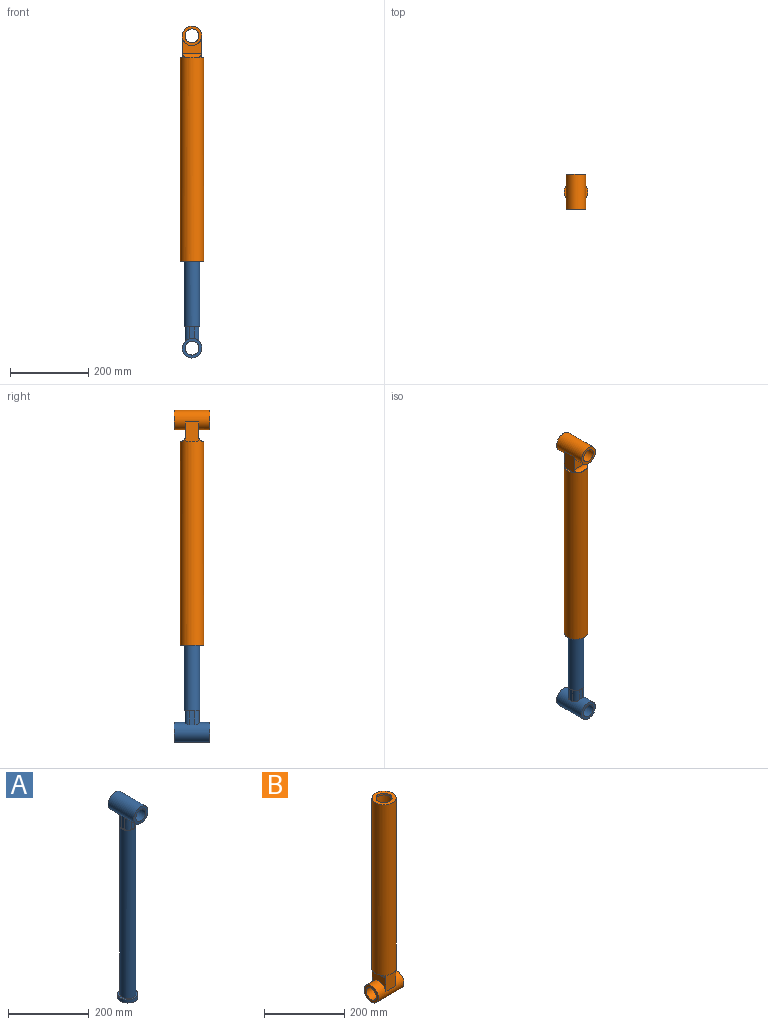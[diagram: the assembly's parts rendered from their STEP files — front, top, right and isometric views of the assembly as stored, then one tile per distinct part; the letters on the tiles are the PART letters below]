
ASSEMBLY  parts=2 mates=1
PART A: 24 faces, bbox 50.2x90x600 mm
  f0: cylinder r=17.5mm len=90mm, axis (0,-1,0), area 9896mm2, adj f18,f19
  f1: cylinder r=25mm len=90mm, axis (0,1,0), area 13084.8mm2, adj f4,f5,f6,f7,f18,f19,f20,f21
  f2: cylinder r=25mm len=50mm, axis (0,0,1), area 1570.8mm2, adj f12,f13
  f3: cylinder r=20mm len=510mm, axis (0,0,1), area 64088.5mm2, adj f8,f9,f10,f11,f13,f14,f15,f16
  f4: plane 36.96x11.71mm, normal (1,0,0), area 432.8mm2, adj f1,f8,f20,f21
  f5: plane 30.66x11mm, normal (0,1,0), area 332.2mm2, adj f1,f11,f20,f23
  f6: plane 37.34x11.71mm, normal (-1,0,0), area 437.2mm2, adj f1,f10,f22,f23
  f7: plane 30.66x11mm, normal (0,-1,0), area 332.2mm2, adj f1,f9,f21,f22
  f8: plane 27.16x5.32mm, normal (0,0,1), area 36.4mm2, adj f3,f4,f20,f21
  f9: plane 25.27x4.5mm, normal (0,0,1), area 28.9mm2, adj f3,f7,f21,f22
  f10: plane 27.16x5.32mm, normal (0,0,1), area 36.4mm2, adj f3,f6,f22,f23
  f11: plane 25.27x4.5mm, normal (0,0,1), area 28.9mm2, adj f3,f5,f20,f23
  f12: plane 50x50mm, normal (0,0,-1), area 1963.5mm2, adj f2
  f13: plane 50x50mm, normal (0,0,1), area 706.9mm2, adj f2,f3
  f14: plane 2.05x1.92mm, normal (0,0,-1), area 0.1mm2, adj f3,f22
  f15: plane 2.05x1.92mm, normal (0,0,-1), area 0.1mm2, adj f3,f21
  f16: plane 2.05x1.92mm, normal (0,0,-1), area 0.1mm2, adj f3,f20
  f17: plane 2.05x1.92mm, normal (0,0,-1), area 0.1mm2, adj f3,f23
  f18: plane 50x50mm, normal (0,-1,0), area 1001.4mm2, adj f0,f1
  f19: plane 50x50mm, normal (0,1,0), area 1001.4mm2, adj f0,f1
  f20: cylinder r=12mm len=36.96mm, axis (0,0,-1), area 636.4mm2, adj f1,f4,f5,f8,f11,f16
  f21: cylinder r=12mm len=36.96mm, axis (0,0,-1), area 636.4mm2, adj f1,f4,f7,f8,f9,f15
  f22: cylinder r=12mm len=37.34mm, axis (0,0,-1), area 640.9mm2, adj f1,f6,f7,f9,f10,f14
  f23: cylinder r=12mm len=37.34mm, axis (0,0,-1), area 640.9mm2, adj f1,f5,f6,f10,f11,f17
PART B: 20 faces, bbox 90x60x600 mm
  f0: cylinder r=25mm len=90mm, axis (1,0,0), area 11782.9mm2, adj f5,f6,f7,f8,f16,f17
  f1: cylinder r=17.5mm len=90mm, axis (1,0,0), area 9896mm2, adj f16,f17
  f2: cylinder r=25mm len=510mm, axis (0,0,1), area 80110.6mm2, adj f14,f15
  f3: cylinder r=20mm len=40mm, axis (0,0,1), area 628.3mm2, adj f13,f14
  f4: cylinder r=30mm len=530mm, axis (0,0,1), area 98133.3mm2, adj f6,f8,f9,f10,f11,f12,f13,f18
  f5: plane 48.73x39.41mm, normal (1,0,0), area 1216mm2, adj f0,f6,f8,f19
  f6: plane 49.41x35mm, normal (0,-1,0), area 1729.3mm2, adj f0,f4,f5,f7,f12
  f7: plane 48.73x39.41mm, normal (-1,0,0), area 1216mm2, adj f0,f6,f8,f18
  f8: plane 49.41x35mm, normal (0,1,0), area 1729.3mm2, adj f0,f4,f5,f7,f10
  f9: plane 23.98x2.5mm, normal (0,0,-1), area 40.3mm2, adj f4,f19
  f10: plane 35x5.63mm, normal (0,0,-1), area 134.1mm2, adj f4,f8
  f11: plane 23.98x2.5mm, normal (0,0,-1), area 40.3mm2, adj f4,f18
  f12: plane 35x5.63mm, normal (0,0,-1), area 134.1mm2, adj f4,f6
  f13: plane 60x60mm, normal (0,0,1), area 1570.8mm2, adj f3,f4
  f14: plane 50x50mm, normal (0,0,-1), area 706.9mm2, adj f2,f3
  f15: plane 50x50mm, normal (0,0,1), area 1963.5mm2, adj f2
  f16: plane 50x50mm, normal (-1,0,0), area 1001.4mm2, adj f0,f1
  f17: plane 50x50mm, normal (1,0,0), area 1001.4mm2, adj f0,f1
  f18: cylinder r=10mm len=48.73mm, axis (0,-1,0), area 652.8mm2, adj f4,f7,f11
  f19: cylinder r=10mm len=48.73mm, axis (0,1,0), area 652.8mm2, adj f4,f5,f9
PLACE A rot(axis=(1,0,0),180deg) t=(-14.61,0,-317.38)mm
PLACE B rot(axis=(-0.71,-0.71,0),180deg) t=(0,0,-55)mm
MATE slider A.f2 <-> B.f2  axis (0,0,-1) through (0,0,-486.95)mm
